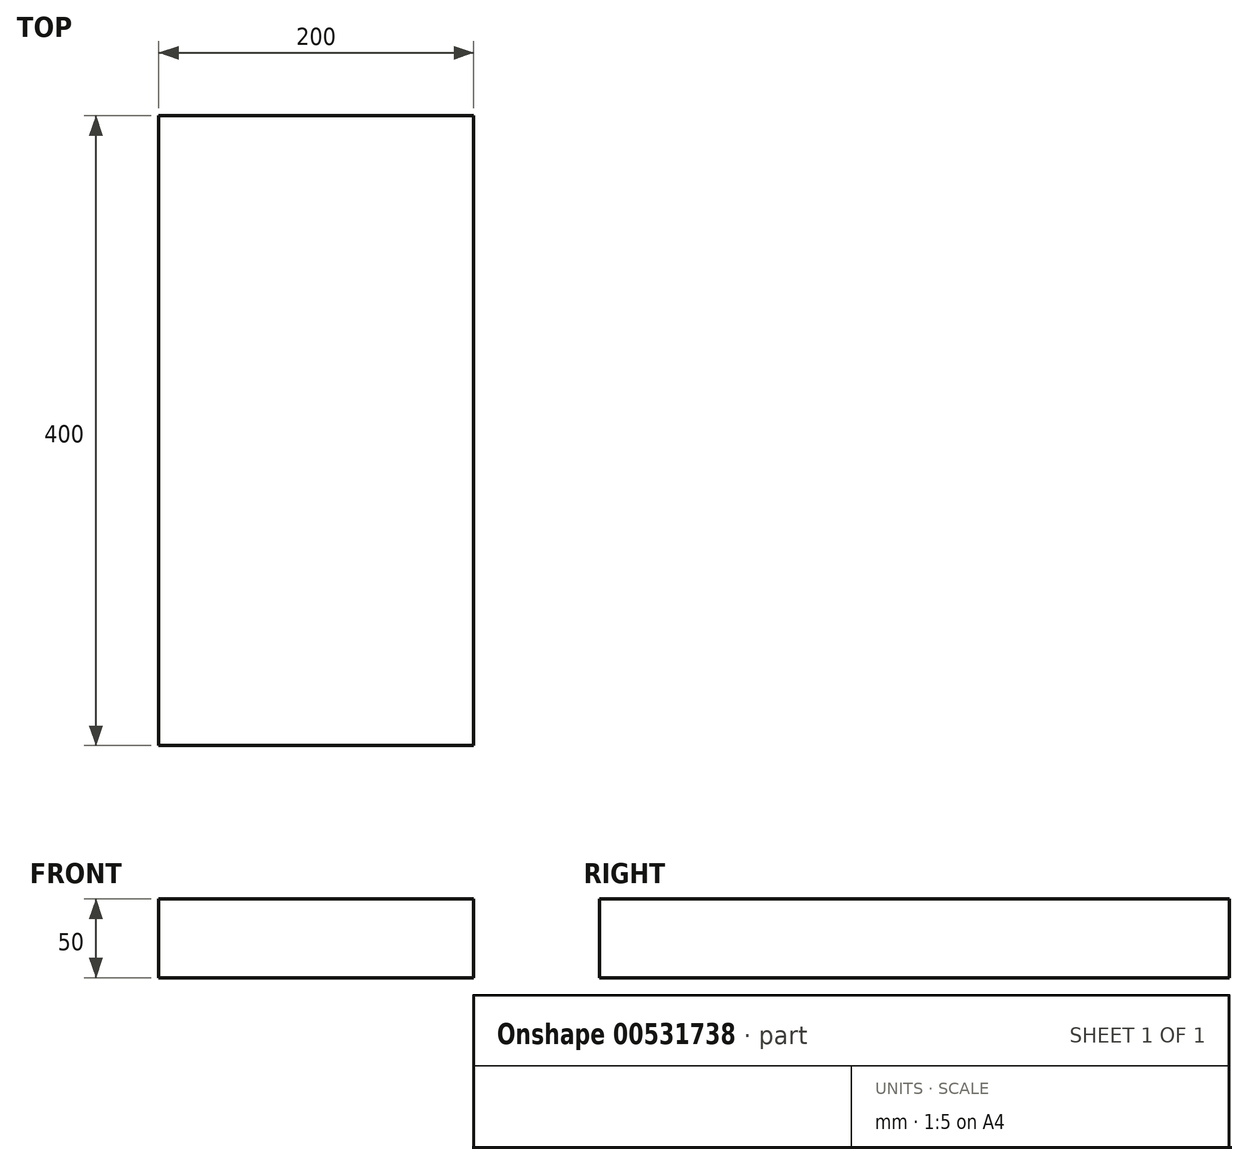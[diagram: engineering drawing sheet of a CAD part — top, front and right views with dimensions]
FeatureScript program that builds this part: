
annotation { "Feature Type Name" : "Feature", "Feature Type Description" : "" }
export const myFeature = defineFeature(function(context is Context, id is Id, definition is map)
    precondition{}
    {
        {
            var Q0;
            Q0=qCreatedBy(makeId("Front.planeOp"),FACE);
            var sketch = newSketch(context, id + "F0", { "sketchPlane" : qUnion([Q0])});
            skLineSegment(sketch, "E0.bottom", {"start": v(-102.97, 25.96) * mm, "end": v(97.03, 25.96) * mm});
            skLineSegment(sketch, "E0.top", {"start": v(-102.97, -24.04) * mm, "end": v(97.03, -24.04) * mm});
            skLineSegment(sketch, "E0.left", {"start": v(-102.97, 25.96) * mm, "end": v(-102.97, -24.04) * mm});
            skLineSegment(sketch, "E0.right", {"start": v(97.03, 25.96) * mm, "end": v(97.03, -24.04) * mm});
            skSolve(sketch);
        }
        {
            var Q0;
            Q0=makeQuery(id+"F0.imprint","IMPRINT",FACE,{"disambiguationData":[TD([[makeQuery(id+"F0.imprint","IMPRINT",EDGE,{"derivedFrom":sQuery(id+"F0.wireOp",EDGE,"E0.bottom")}),-1.0]])]});
            extrude(context, id + "F1", {"entities" : qUnion([Q0]), "depth" : 400 * mm, "offsetDistance" : 25 * mm});
        }
    });
